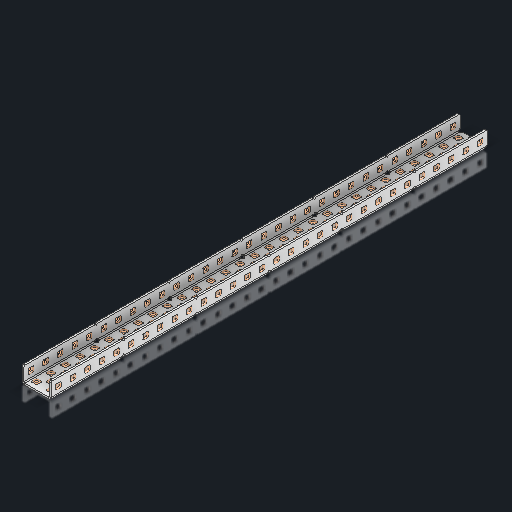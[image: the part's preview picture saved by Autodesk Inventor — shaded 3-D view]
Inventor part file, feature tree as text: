
AUTODESK INVENTOR PART (.ipt)
format: ipt  version: 2023.2 (Build 272271030, 271C)  size: 2,606,592 bytes
history: native  units: in
note: dims shown in document units (in); Inventor stores cm internally (conversion verified against a paired STEP export)
features: other x306, sketch x10, sheet_metal_op x1
ambient origin geometry x8: Origin, YZ Plane, XZ Plane, XY Plane, X Axis, Y Axis, Z Axis, Center Point
bodies: Solid1 (feature_tree)
feature tree (317):
  other  "Alu C 1x2x1x30_MIR.ipt"
  other  "Solid1::Alu C 1x2x1x30_MIR.ipt"
  other  "TaggingFeature1"
  sketch  "Sketch1"  dims[d0=0.3937in]
  sketch  "Sketch2"  dims[d1=0.0625in]
  sketch  "Sketch3"
  sketch  "Sketch7"
  other  "Flange Pattern Sketch"
  sketch  "Sketch8"
  sketch  "Sketch9"
  sheet_metal_op  "Body Pattern Sketch"
  sketch  "Sketch15"
  sketch  "Sketch16"
  other  "Arc Length"
  sketch  "Sketch13"
  sketch  "Sketch14"
  other  "Flange Pattern Plane"
  other  "Srf1"
  other  "Srf2"
  other  "Srf3"
  other  "Srf4"
  other  "Srf5"
  other  "Srf6"
  other  "Srf7"
  other  "Srf8"
  other  "Srf9"
  other  "Srf10"
  other  "Srf11"
  other  "Srf12"
  other  "Srf13"
  other  "Srf14"
  other  "Srf15"
  other  "Srf16"
  other  "Srf17"
  other  "Srf18"
  other  "Srf19"
  other  "Srf20"
  other  "Srf21"
  other  "Srf22"
  other  "Srf23"
  other  "Srf24"
  other  "Srf25"
  other  "Srf26"
  other  "Srf27"
  other  "Srf28"
  other  "Srf29"
  other  "Srf30"
  other  "Srf31"
  other  "Srf32"
  other  "Srf33"
  other  "Srf34"
  other  "Srf35"
  other  "Srf36"
  other  "Srf37"
  other  "Srf38"
  other  "Srf39"
  other  "Srf40"
  other  "Srf41"
  other  "Srf42"
  other  "Srf43"
  other  "Srf44"
  other  "Srf45"
  other  "Srf46"
  other  "Srf47"
  other  "Srf48"
  other  "Srf49"
  other  "Srf50"
  other  "Srf51"
  other  "Srf52"
  other  "Srf53"
  other  "Srf54"
  other  "Srf55"
  other  "Srf56"
  other  "Srf57"
  other  "Srf58"
  other  "Srf59"
  other  "Srf60"
  other  "Srf61"
  other  "Srf62"
  other  "Srf63"
  other  "Srf64"
  other  "Srf65"
  other  "Srf66"
  other  "Srf67"
  other  "Srf68"
  other  "Srf69"
  other  "Srf70"
  other  "Srf71"
  other  "Srf72"
  other  "Srf73"
  other  "Srf74"
  other  "Srf75"
  other  "Srf76"
  other  "Srf77"
  other  "Srf78"
  other  "Srf79"
  other  "Srf80"
  other  "Srf81"
  other  "Srf82"
  other  "Srf83"
  other  "Srf84"
  other  "Srf85"
  other  "Srf86"
  other  "Srf87"
  other  "Srf88"
  other  "Srf89"
  other  "Srf90"
  other  "Srf91"
  other  "Srf92"
  other  "Srf93"
  other  "Srf94"
  other  "Srf95"
  other  "Srf96"
  other  "Srf97"
  other  "Srf98"
  other  "Srf99"
  other  "Srf100"
  other  "Srf101"
  other  "Srf102"
  other  "Srf103"
  other  "Srf104"
  other  "Srf105"
  other  "Srf106"
  other  "Srf107"
  other  "Srf108"
  other  "Srf109"
  other  "Srf110"
  other  "Srf111"
  other  "Srf112"
  other  "Srf113"
  other  "Srf114"
  other  "Srf115"
  other  "Srf116"
  other  "Srf117"
  other  "Srf118"
  other  "Srf119"
  other  "Srf120"
  other  "Srf121"
  other  "Srf122"
  other  "Srf123"
  other  "Srf124"
  other  "Srf125"
  other  "Srf126"
  other  "Srf127"
  other  "Srf128"
  other  "Srf129"
  other  "Srf130"
  other  "Srf131"
  other  "Srf132"
  other  "Srf133"
  other  "Srf134"
  other  "Srf135"
  other  "Srf136"
  other  "Srf137"
  other  "Srf138"
  other  "Srf139"
  other  "Srf140"
  other  "Srf141"
  other  "Srf142"
  other  "Srf143"
  other  "Srf144"
  other  "Srf145"
  other  "Srf146"
  other  "Srf147"
  other  "Srf148"
  other  "Srf149"
  other  "Srf150"
  other  "Srf1::Derived"
  other  "Srf2::Derived"
  other  "Srf3::Derived"
  other  "Srf4::Derived"
  other  "Srf5::Derived"
  other  "Srf6::Derived"
  other  "Srf7::Derived"
  other  "Srf8::Derived"
  other  "Srf9::Derived"
  other  "Srf10::Derived"
  other  "Srf11::Derived"
  other  "Srf12::Derived"
  other  "Srf13::Derived"
  other  "Srf14::Derived"
  other  "Srf15::Derived"
  other  "Srf16::Derived"
  other  "Srf17::Derived"
  other  "Srf18::Derived"
  other  "Srf19::Derived"
  other  "Srf20::Derived"
  other  "Srf21::Derived"
  other  "Srf22::Derived"
  other  "Srf23::Derived"
  other  "Srf24::Derived"
  other  "Srf25::Derived"
  other  "Srf26::Derived"
  other  "Srf27::Derived"
  other  "Srf28::Derived"
  other  "Srf29::Derived"
  other  "Srf30::Derived"
  other  "Srf31::Derived"
  other  "Srf32::Derived"
  other  "Srf33::Derived"
  other  "Srf34::Derived"
  other  "Srf35::Derived"
  other  "Srf36::Derived"
  other  "Srf37::Derived"
  other  "Srf38::Derived"
  other  "Srf39::Derived"
  other  "Srf40::Derived"
  other  "Srf41::Derived"
  other  "Srf42::Derived"
  other  "Srf43::Derived"
  other  "Srf44::Derived"
  other  "Srf45::Derived"
  other  "Srf46::Derived"
  other  "Srf47::Derived"
  other  "Srf48::Derived"
  other  "Srf49::Derived"
  other  "Srf50::Derived"
  other  "Srf51::Derived"
  other  "Srf52::Derived"
  other  "Srf53::Derived"
  other  "Srf54::Derived"
  other  "Srf55::Derived"
  other  "Srf56::Derived"
  other  "Srf57::Derived"
  other  "Srf58::Derived"
  other  "Srf59::Derived"
  other  "Srf60::Derived"
  other  "Srf61::Derived"
  other  "Srf62::Derived"
  other  "Srf63::Derived"
  other  "Srf64::Derived"
  other  "Srf65::Derived"
  other  "Srf66::Derived"
  other  "Srf67::Derived"
  other  "Srf68::Derived"
  other  "Srf69::Derived"
  other  "Srf70::Derived"
  other  "Srf71::Derived"
  other  "Srf72::Derived"
  other  "Srf73::Derived"
  other  "Srf74::Derived"
  other  "Srf75::Derived"
  other  "Srf76::Derived"
  other  "Srf77::Derived"
  other  "Srf78::Derived"
  other  "Srf79::Derived"
  other  "Srf80::Derived"
  other  "Srf81::Derived"
  other  "Srf82::Derived"
  other  "Srf83::Derived"
  other  "Srf84::Derived"
  other  "Srf85::Derived"
  other  "Srf86::Derived"
  other  "Srf87::Derived"
  other  "Srf88::Derived"
  other  "Srf89::Derived"
  other  "Srf90::Derived"
  other  "Srf91::Derived"
  other  "Srf92::Derived"
  other  "Srf93::Derived"
  other  "Srf94::Derived"
  other  "Srf95::Derived"
  other  "Srf96::Derived"
  other  "Srf97::Derived"
  other  "Srf98::Derived"
  other  "Srf99::Derived"
  other  "Srf100::Derived"
  other  "Srf101::Derived"
  other  "Srf102::Derived"
  other  "Srf103::Derived"
  other  "Srf104::Derived"
  other  "Srf105::Derived"
  other  "Srf106::Derived"
  other  "Srf107::Derived"
  other  "Srf108::Derived"
  other  "Srf109::Derived"
  other  "Srf110::Derived"
  other  "Srf111::Derived"
  other  "Srf112::Derived"
  other  "Srf113::Derived"
  other  "Srf114::Derived"
  other  "Srf115::Derived"
  other  "Srf116::Derived"
  other  "Srf117::Derived"
  other  "Srf118::Derived"
  other  "Srf119::Derived"
  other  "Srf120::Derived"
  other  "Srf121::Derived"
  other  "Srf122::Derived"
  other  "Srf123::Derived"
  other  "Srf124::Derived"
  other  "Srf125::Derived"
  other  "Srf126::Derived"
  other  "Srf127::Derived"
  other  "Srf128::Derived"
  other  "Srf129::Derived"
  other  "Srf130::Derived"
  other  "Srf131::Derived"
  other  "Srf132::Derived"
  other  "Srf133::Derived"
  other  "Srf134::Derived"
  other  "Srf135::Derived"
  other  "Srf136::Derived"
  other  "Srf137::Derived"
  other  "Srf138::Derived"
  other  "Srf139::Derived"
  other  "Srf140::Derived"
  other  "Srf141::Derived"
  other  "Srf142::Derived"
  other  "Srf143::Derived"
  other  "Srf144::Derived"
  other  "Srf145::Derived"
  other  "Srf146::Derived"
  other  "Srf147::Derived"
  other  "Srf148::Derived"
  other  "Srf149::Derived"
  other  "Srf150::Derived"
